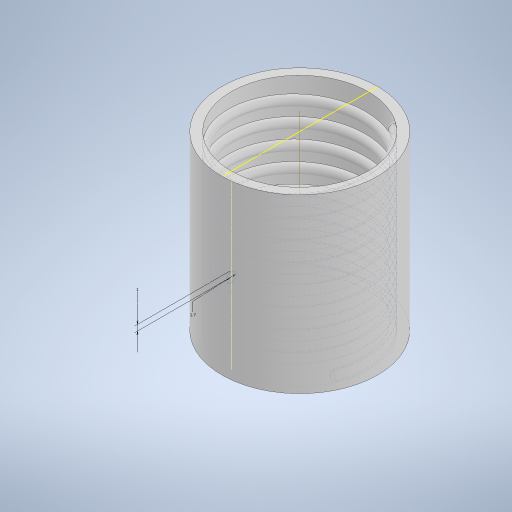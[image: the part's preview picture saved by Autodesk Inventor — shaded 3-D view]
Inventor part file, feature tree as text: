
AUTODESK INVENTOR PART (.ipt)
format: ipt  version: 2024.1 (Build 281209000, 209)  size: 628,736 bytes
history: native  units: mm
features: sketch x4, helix x3, fillet x3, projected_geometry x3, extrude x2
ambient origin geometry x8: Origin, YZ Plane, XZ Plane, XY Plane, X Axis, Y Axis, Z Axis, Center Point
bodies: Solid1 (feature_tree), Solid2 (feature_tree)
feature tree (15):
  extrude  "Extrusion1"  Depth=18.0mm
  helix  "Coil1"  [1 undecoded]
  fillet  "Fillet1"  Radius=2.15mm
  extrude  "Extrusion2"  Depth=1.0mm
  sketch  "Sketch4"  dims[d20=1.0mm d21=3.4mm d22=13.0mm d23=50.0mm d24=0.0mm d25=90.0deg d26=90.0deg d27=0.0mm d28=0.0mm d29=3.4mm d30=15.0mm d31=50.0mm d32=0.0mm d33=90.0deg d34=90.0deg d35=0.0mm d36=0.0mm d37=0.7mm d38=0.7mm]
  helix  "Coil2"  [1 undecoded]
  helix  "Coil3"  [1 undecoded]
  fillet  "Fillet2"  Radius=30.0mm
  fillet  "Fillet3"  Radius=1.7mm
  sketch  "Sketch1"  dims[d0=21.12mm d1=18.0mm d2=14.0mm d3=0.0mm d4=2.15mm]
  sketch  "Sketch2"  dims[d5=2.8mm]
  projected_geometry  "Projected Loop1"
  sketch  "Sketch3"  dims[d6=3.4mm d7=10.0mm d8=50.0mm d9=0.0mm d10=90.0deg d11=90.0deg d12=0.0mm d13=0.0mm d14=1.0mm d15=3.0mm d16=1.4mm d17=30.0mm d18=0.0mm d19=1.7mm]
  projected_geometry  "Projected Loop2"
  projected_geometry  "Projected Loop3"
note: 3 required parameter values undecoded (feature->parameter linkage not recoverable at this tier; creation-order binding heuristic only, values carry confidence <= 0.55)
